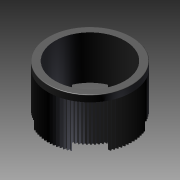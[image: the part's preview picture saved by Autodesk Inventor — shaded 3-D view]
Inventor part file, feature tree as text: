
AUTODESK INVENTOR PART (.ipt)
format: ipt  version: 2014 (Build 180170000, 170)  size: 526,336 bytes
history: native  units: in
note: dims shown in document units (in); Inventor stores cm internally (conversion verified against a paired STEP export)
features: other x7, sketch x5, extrude x4, revolve x1
ambient origin geometry x8: Origin, YZ Plane, XZ Plane, XY Plane, X Axis, Y Axis, Z Axis, Center Point
bodies: Solid1 (feature_tree)
feature tree (17):
  revolve  "Revolution1"  [1 undecoded]
  extrude  "Extrusion1"  Depth=0.709in TaperAngle=0.0deg
  extrude  "Extrusion2"  [1 undecoded]
  extrude  "Extrusion3"  [1 undecoded]
  extrude  "Extrusion4"  [1 undecoded]
  other  "nut_to_body_XY"
  other  "nut_to_body_YZ"
  other  "nut_to_body_ZX"
  other  "nut_to_body_X"
  other  "nut_to_body_Y"
  other  "nut_to_body_Z"
  other  "nut_to_body_Center"
  sketch  "Sketch_1"  dims[d0=360.0deg d1=1.418in d2=0.0in]
  sketch  "Sketch_2"  dims[d3=1.418in d4=0.0in d5=0.709in d6=0.0in]
  sketch  "Sketch_3"  dims[d7=0.709in d8=0.0in]
  sketch  "Sketch_4"
  sketch  "Sketch_5"
note: 4 required parameter values undecoded (feature->parameter linkage not recoverable at this tier; creation-order binding heuristic only, values carry confidence <= 0.55)